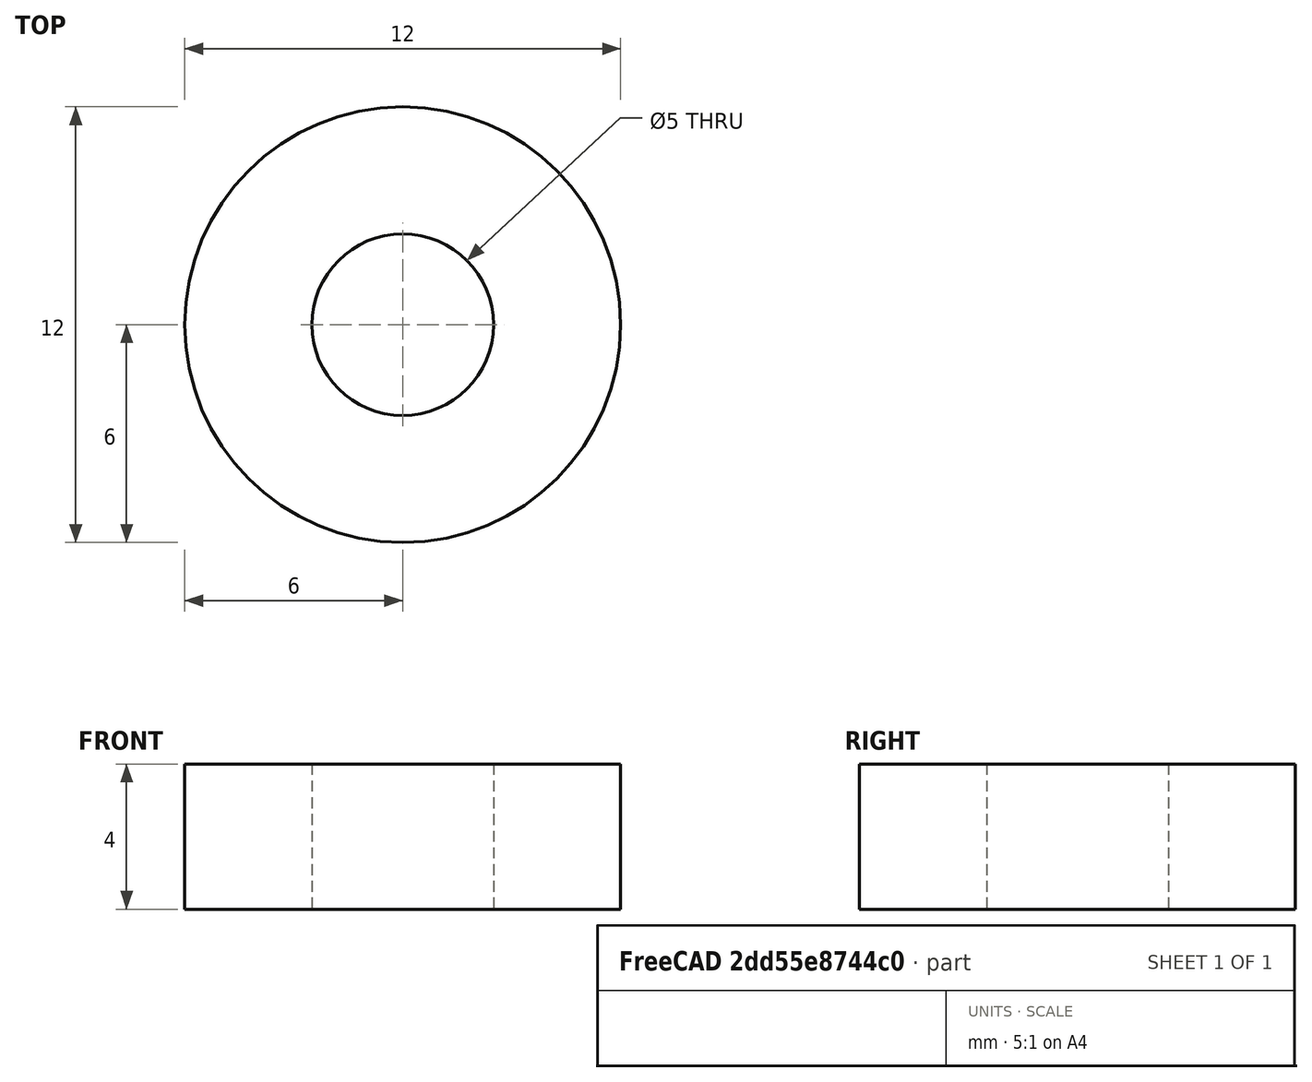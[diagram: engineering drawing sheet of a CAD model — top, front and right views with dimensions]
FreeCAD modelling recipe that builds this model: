
FCSTD DOCUMENT  (FreeCAD 0.14R3700 (Git))
Label: BR_Roulement
License: CC-BY 3.0
LicenseURL: http://creativecommons.org/licenses/by/3.0/
objects: Sketcher::SketchObject×1, Part::Revolution×1, Part::Feature×1
note: 3 computed .brp shape members not serialized (recipe doc carries the construction recipe); baked Part::Feature solids carry a one-line shape summary decoded from their .brp

FEATURE [Sketcher::SketchObject] Sketch  label="roulement"
  Placement = pos=(0,0,0) rot=(1,0,0;1.5708rad)
  sketch-geometry (4):
    g0: LineSegment StartX=-6 StartY=4 StartZ=0 EndX=-2.5 EndY=4 EndZ=0
    g1: LineSegment StartX=-2.5 StartY=4 StartZ=0 EndX=-2.5 EndY=0 EndZ=0
    g2: LineSegment StartX=-2.5 StartY=0 StartZ=0 EndX=-6 EndY=0 EndZ=0
    g3: LineSegment StartX=-6 StartY=0 StartZ=0 EndX=-6 EndY=4 EndZ=0
  constraints (12):
    c: Coincident(g0,g1)
    c: Coincident(g1,g2)
    c: Coincident(g2,g3)
    c: Coincident(g3,g0)
    c: Horizontal(g0)
    c: Horizontal(g2)
    c: Vertical(g1)
    c: Vertical(g3)
    c: PointOnObject(g1,g-1)
    c: DistanceX(g-1,g1) = -2.5
    c: DistanceX(g-1,g2) = -6
    c: DistanceY(g3) = 4
FEATURE [Part::Revolution] Revolve
  Angle = 360
  Axis = (0,0,1)
  Base = (0,0,0)
  Solid = false
  Source = -> Sketch
FEATURE [Part::Feature] Revolve001  label="roulement_copy"
  shape: bbox 12 x 12 x 4 mm, 4 faces, 0 solids (baked)
